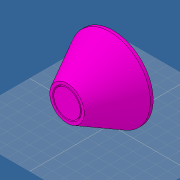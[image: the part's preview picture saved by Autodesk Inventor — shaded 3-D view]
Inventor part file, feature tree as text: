
AUTODESK INVENTOR PART (.ipt)
format: ipt  version: 2019 (Build 230136000, 136)  size: 108,544 bytes
history: native  units: mm
features: sketch x2, extrude x2, revolve x1, other x1
ambient origin geometry x8: Origin, YZ Plane, XZ Plane, XY Plane, X Axis, Y Axis, Z Axis, Center Point
bodies: Volumenkörper1 (feature_tree)
feature tree (6):
  sketch  "Skizze1"  dims[d0=140.0mm d1=50.1mm]
  extrude  "Extrusion1"  Depth=50.1mm
  extrude  "Extrusion2"  Depth=5.0mm TaperAngle=0.0deg
  revolve  "Umdrehung1"
  sketch  "Skizze2"  dims[d2=46.1mm d3=5.0mm d4=0.0mm d5=75.0mm d6=0.0mm d7=5.0mm d8=90.0deg]
  other  "Schnittkanten projizieren1"
